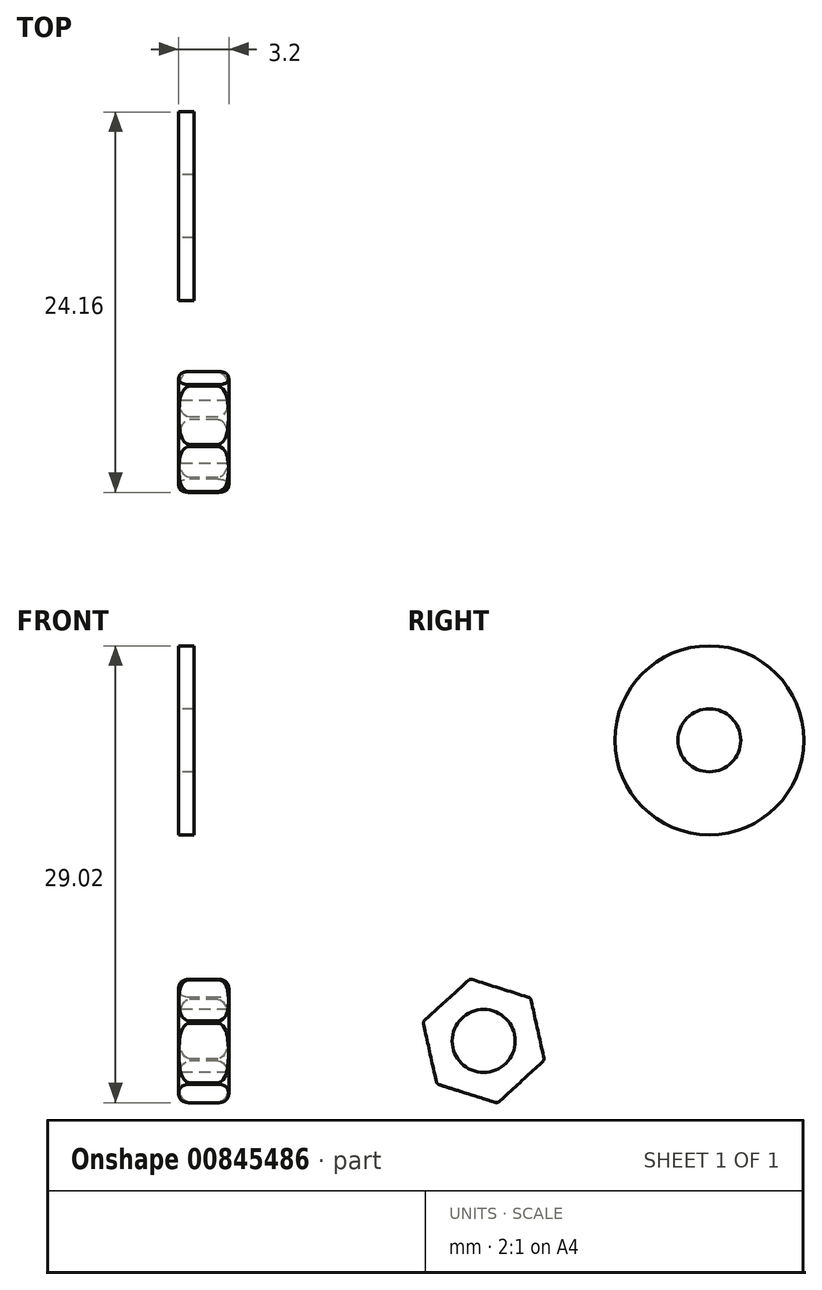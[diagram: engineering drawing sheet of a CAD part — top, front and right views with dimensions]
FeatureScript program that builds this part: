
annotation { "Feature Type Name" : "Feature", "Feature Type Description" : "" }
export const myFeature = defineFeature(function(context is Context, id is Id, definition is map)
    precondition{}
    {
        {
            var Q0;
            Q0=qCreatedBy(makeId("Front.planeOp"),FACE);
            var sketch = newSketch(context, id + "F0", { "sketchPlane" : qUnion([Q0])});
            skLineSegment(sketch, "E0", {"start": v(0, 0) * mm, "end": v(0, 3.5) * mm});
            skLineSegment(sketch, "E1", {"start": v(0, 3.5) * mm, "end": v(2.8, 3.5) * mm});
            skLineSegment(sketch, "E2", {"start": v(2.8, 3.5) * mm, "end": v(2.8, 2) * mm});
            skLineSegment(sketch, "E3", {"start": v(2.8, 2) * mm, "end": v(12.8, 2) * mm});
            skLineSegment(sketch, "E4", {"start": v(12.8, 2) * mm, "end": v(12.8, 0) * mm});
            skLineSegment(sketch, "E5", {"start": v(12.8, 0) * mm, "end": v(0, 0) * mm});
            skSolve(sketch);
        }
        {
            var Q0;
            Q0=qSketchRegion(id+"F0",true);
            var Q1;
            Q1=sQuery(id+"F0.wireOp",EDGE,"E5");
            revolve(context, id + "F1", {"entities" : qUnion([Q0]), "axis" : qUnion([Q1]), "revolveType" : RevolveType.FULL});
        }
        {
            var Q0;
            Q0=makeQuery(id+"F1.opRevolve","SWEPT_FACE",FACE,{"disambiguationData":[OSD([sQuery(id+"F0.wireOp",EDGE,"E0")])]});
            var sketch = newSketch(context, id + "F2", { "sketchPlane" : qUnion([Q0])});
            skLineSegment(sketch, "E6.left", {"start": v(0.5, -3.46) * mm, "end": v(0.5, 3.46) * mm});
            skLineSegment(sketch, "E6.right", {"start": v(-0.5, -3.46) * mm, "end": v(-0.5, 3.46) * mm});
            skPoint(sketch, "E6.middle", {"position": v(0, 0) * mm});
            skArc(sketch, "E7", {"start": v(-0.5, -3.46) * mm, "mid": v(0, -3.5) * mm, "end": v(0.5, -3.46) * mm});
            skArc(sketch, "E8.trimOffspring", {"start": v(0.5, 3.46) * mm, "mid": v(0, 3.5) * mm, "end": v(-0.5, 3.46) * mm});
            skSolve(sketch);
        }
        {
            var Q0;
            Q0=qSketchRegion(id+"F2",true);
            extrude(context, id + "F3", {"entities" : qUnion([Q0]), "operationType" : NewBodyOperationType.REMOVE, "oppositeDirection" : true, "depth" : 1.4 * mm});
        }
        {
            var Q0;
            Q0=qCreatedBy(makeId("Right.planeOp"),FACE);
            var sketch = newSketch(context, id + "F4", { "sketchPlane" : qUnion([Q0])});
            skCircle(sketch, "E9", {"center": v(-39.12, 7.47) * mm, "radius": 4 * mm});
            skCircle(sketch, "E10", {"center": v(-39.12, 7.47) * mm, "radius": 2 * mm});
            skSolve(sketch);
        }
        {
            var Q0;
            Q0=qSketchRegion(id+"F4",true);
            extrude(context, id + "F5", {"entities" : qUnion([Q0]), "depth" : 3.2 * mm});
        }
        {
            var Q0;
            Q0=makeQuery(id+"F5.opExtrude","CAP_EDGE",EDGE,{"disambiguationData":[OSD([sQuery(id+"F4.wireOp",EDGE,"E9")])],"isStart":false});
            var Q1;
            Q1=makeQuery(id+"F5.opExtrude","CAP_EDGE",EDGE,{"disambiguationData":[OSD([sQuery(id+"F4.wireOp",EDGE,"E9")])],"isStart":true});
            fillet(context, id + "F6", {"entities" : qUnion([Q0, Q1]), "radius" : 0.7 * mm, "tangentPropagation" : true, "allowEdgeOverflow" : false});
        }
        {
            var Q0;
            Q0=makeQuery(id+"F5.opExtrude","CAP_FACE",FACE,{"disambiguationData":[OSD([sQuery(id+"F4.wireOp",EDGE,"E9"),sQuery(id+"F4.wireOp",EDGE,"E10")])],"isStart":false});
            var sketch = newSketch(context, id + "F7", { "sketchPlane" : qUnion([Q0])});
            skCircle(sketch, "E11.cCircle", {"center": v(-39.12, 7.47) * mm, "radius": 4.04 * mm, "construction": true});
            skLineSegment(sketch, "E11.0", {"start": v(-35.26, 6.25) * mm, "end": v(-38.24, 3.52) * mm});
            skLineSegment(sketch, "E11.1", {"start": v(-38.24, 3.52) * mm, "end": v(-42.1, 4.74) * mm});
            skLineSegment(sketch, "E11.2", {"start": v(-42.1, 4.74) * mm, "end": v(-42.97, 8.68) * mm});
            skLineSegment(sketch, "E11.3", {"start": v(-42.97, 8.68) * mm, "end": v(-39.99, 11.41) * mm});
            skLineSegment(sketch, "E11.4", {"start": v(-39.99, 11.41) * mm, "end": v(-36.14, 10.2) * mm});
            skLineSegment(sketch, "E11.5", {"start": v(-36.14, 10.2) * mm, "end": v(-35.26, 6.25) * mm});
            skSolve(sketch);
        }
        {
            var Q0;
            Q0=qSketchRegion(id+"F7",true);
            extrude(context, id + "F8", {"entities" : qUnion([Q0]), "operationType" : NewBodyOperationType.INTERSECT, "endBound" : BoundingType.THROUGH_ALL, "oppositeDirection" : true, "depth" : 25 * mm});
        }
        {
            var Q0;
            Q0=qCreatedBy(makeId("Right.planeOp"),FACE);
            var sketch = newSketch(context, id + "F9", { "sketchPlane" : qUnion([Q0])});
            skCircle(sketch, "E12", {"center": v(-24.79, 26.57) * mm, "radius": 6 * mm});
            skCircle(sketch, "E13", {"center": v(-24.79, 26.57) * mm, "radius": 2 * mm});
            skSolve(sketch);
        }
        {
            var Q0;
            Q0=qSketchRegion(id+"F9",true);
            extrude(context, id + "F10", {"entities" : qUnion([Q0]), "depth" : 1 * mm});
        }
    });
